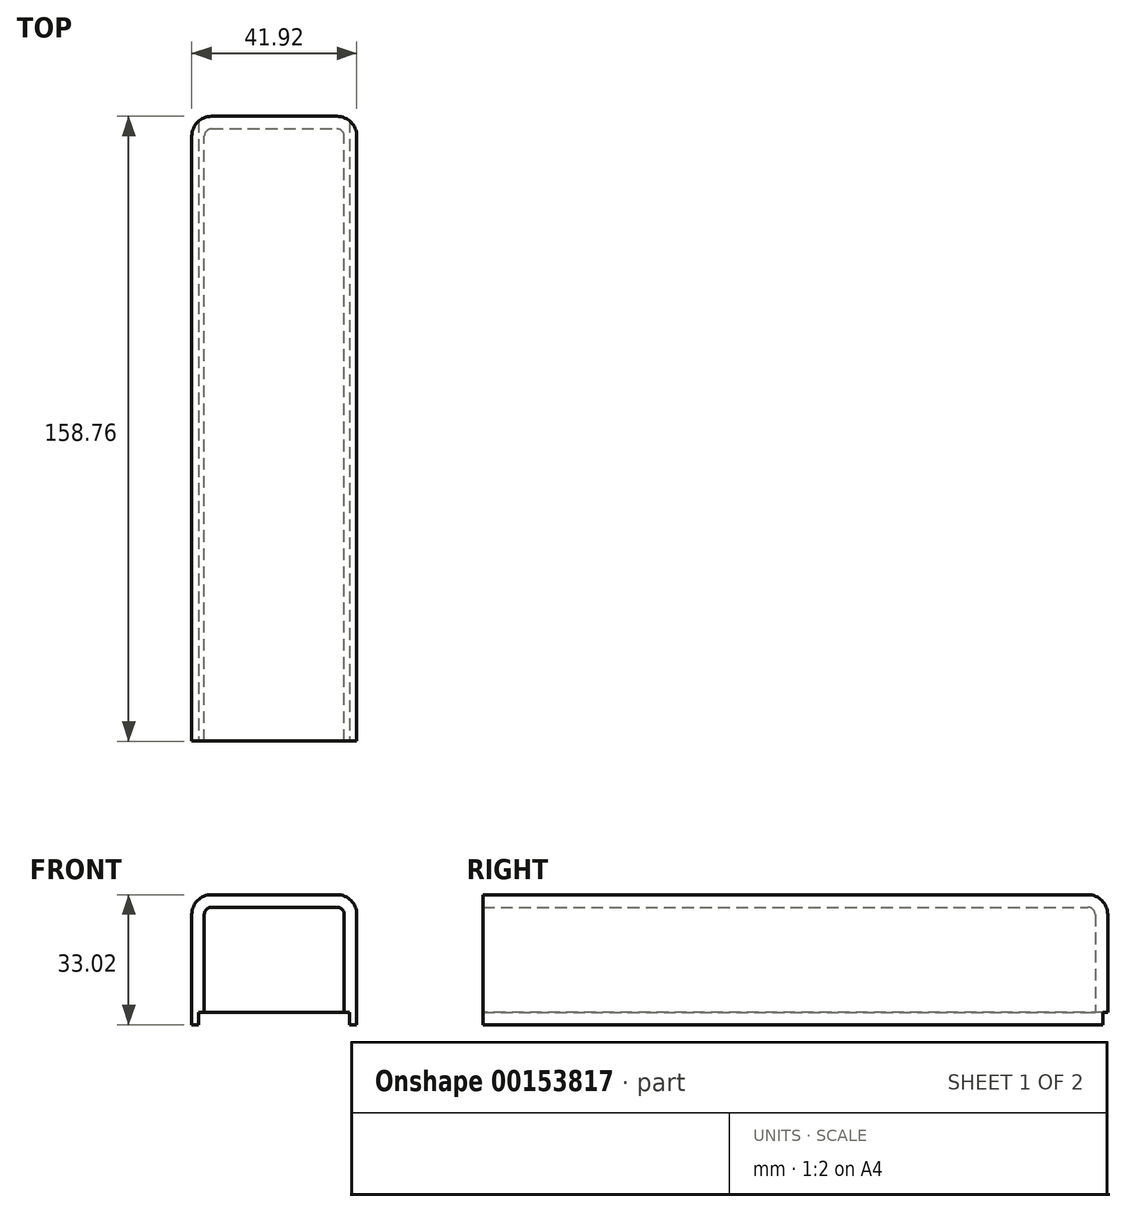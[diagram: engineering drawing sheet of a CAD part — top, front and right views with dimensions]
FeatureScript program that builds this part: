
annotation { "Feature Type Name" : "Feature", "Feature Type Description" : "" }
export const myFeature = defineFeature(function(context is Context, id is Id, definition is map)
    precondition{}
    {
        {
            var Q0;
            Q0=qCreatedBy(makeId("Top.planeOp"),FACE);
            var sketch = newSketch(context, id + "F0", { "sketchPlane" : qUnion([Q0])});
            skLineSegment(sketch, "E0.bottom", {"start": v(15.96, 79.38) * mm, "end": v(-15.95, 79.38) * mm});
            skLineSegment(sketch, "E0.top", {"start": v(20.95, -79.38) * mm, "end": v(-20.96, -79.38) * mm});
            skLineSegment(sketch, "E0.left", {"start": v(20.96, 74.38) * mm, "end": v(20.95, -79.38) * mm});
            skLineSegment(sketch, "E0.right", {"start": v(-20.95, 74.38) * mm, "end": v(-20.96, -79.38) * mm});
            skPoint(sketch, "E0.middle", {"position": v(0, 0) * mm});
            skPoint(sketch, "E1.visualSharp", {"position": v(-20.95, 79.38) * mm});
            skArc(sketch, "E1.filletArc", {"start": v(-15.95, 79.38) * mm, "mid": v(-19.5, 77.91) * mm, "end": v(-20.95, 74.38) * mm});
            skPoint(sketch, "E2.visualSharp", {"position": v(20.96, 79.38) * mm});
            skArc(sketch, "E2.filletArc", {"start": v(20.96, 74.38) * mm, "mid": v(19.5, 77.91) * mm, "end": v(15.96, 79.38) * mm});
            skSolve(sketch);
        }
        {
            var Q0;
            Q0 = qSketchRegion(id + "F0", true);
            extrude(context, id + "F1", {"entities" : qUnion([Q0]), "depth" : 33.02 * mm});
        }
        {
            var Q0;
            Q0=makeQuery(id+"F1.opExtrude","CAP_EDGE",EDGE,{"disambiguationData":[OSD([sQuery(id+"F0.wireOp",EDGE,"E0.right")])],"isStart":false});
            var Q1;
            Q1=makeQuery(id+"F1.opExtrude","CAP_EDGE",EDGE,{"disambiguationData":[OSD([sQuery(id+"F0.wireOp",EDGE,"E0.bottom")])],"isStart":false});
            fillet(context, id + "F2", {"entities" : qUnion([Q0, Q1]), "radius" : 5 * mm, "tangentPropagation" : true, "allowEdgeOverflow" : false});
        }
        {
            var Q0;
            Q0=makeQuery(id+"F1.opExtrude","SWEPT_FACE",FACE,{"disambiguationData":[OSD([sQuery(id+"F0.wireOp",EDGE,"E0.top")])]});
            var Q1;
            Q1=makeQuery(id+"F1.opExtrude","CAP_FACE",FACE,{"disambiguationData":[OSD([sQuery(id+"F0.wireOp",EDGE,"E0.bottom"),sQuery(id+"F0.wireOp",EDGE,"E0.top"),sQuery(id+"F0.wireOp",EDGE,"E0.left"),sQuery(id+"F0.wireOp",EDGE,"E0.right"),sQuery(id+"F0.wireOp",EDGE,"E1.filletArc"),sQuery(id+"F0.wireOp",EDGE,"E2.filletArc")])],"isStart":true});
            shell(context, id + "F3", {"entities" : qUnion([Q0, Q1]), "thickness" : 3.17 * mm});
        }
        {
            var Q0;
            Q0=makeQuery(id+"F1.opExtrude","CAP_FACE",FACE,{"disambiguationData":[OSD([sQuery(id+"F0.wireOp",EDGE,"E0.bottom"),sQuery(id+"F0.wireOp",EDGE,"E0.top"),sQuery(id+"F0.wireOp",EDGE,"E0.left"),sQuery(id+"F0.wireOp",EDGE,"E0.right"),sQuery(id+"F0.wireOp",EDGE,"E1.filletArc"),sQuery(id+"F0.wireOp",EDGE,"E2.filletArc")])],"isStart":true});
            var sketch = newSketch(context, id + "F4", { "sketchPlane" : qUnion([Q0])});
            skLineSegment(sketch, "E3.bottom", {"start": v(19.18, -100.84) * mm, "end": v(-19.18, -100.84) * mm});
            skLineSegment(sketch, "E3.top", {"start": v(19.18, 100.84) * mm, "end": v(-19.18, 100.84) * mm});
            skLineSegment(sketch, "E3.left", {"start": v(19.18, -100.84) * mm, "end": v(19.18, 100.84) * mm});
            skLineSegment(sketch, "E3.right", {"start": v(-19.18, -100.84) * mm, "end": v(-19.18, 100.84) * mm});
            skPoint(sketch, "E3.middle", {"position": v(0, 0) * mm});
            skSolve(sketch);
        }
        {
            var Q0;
            Q0 = qSketchRegion(id + "F4", true);
            extrude(context, id + "F5", {"entities" : qUnion([Q0]), "operationType" : NewBodyOperationType.REMOVE, "oppositeDirection" : true, "depth" : 3.17 * mm});
        }
    });
